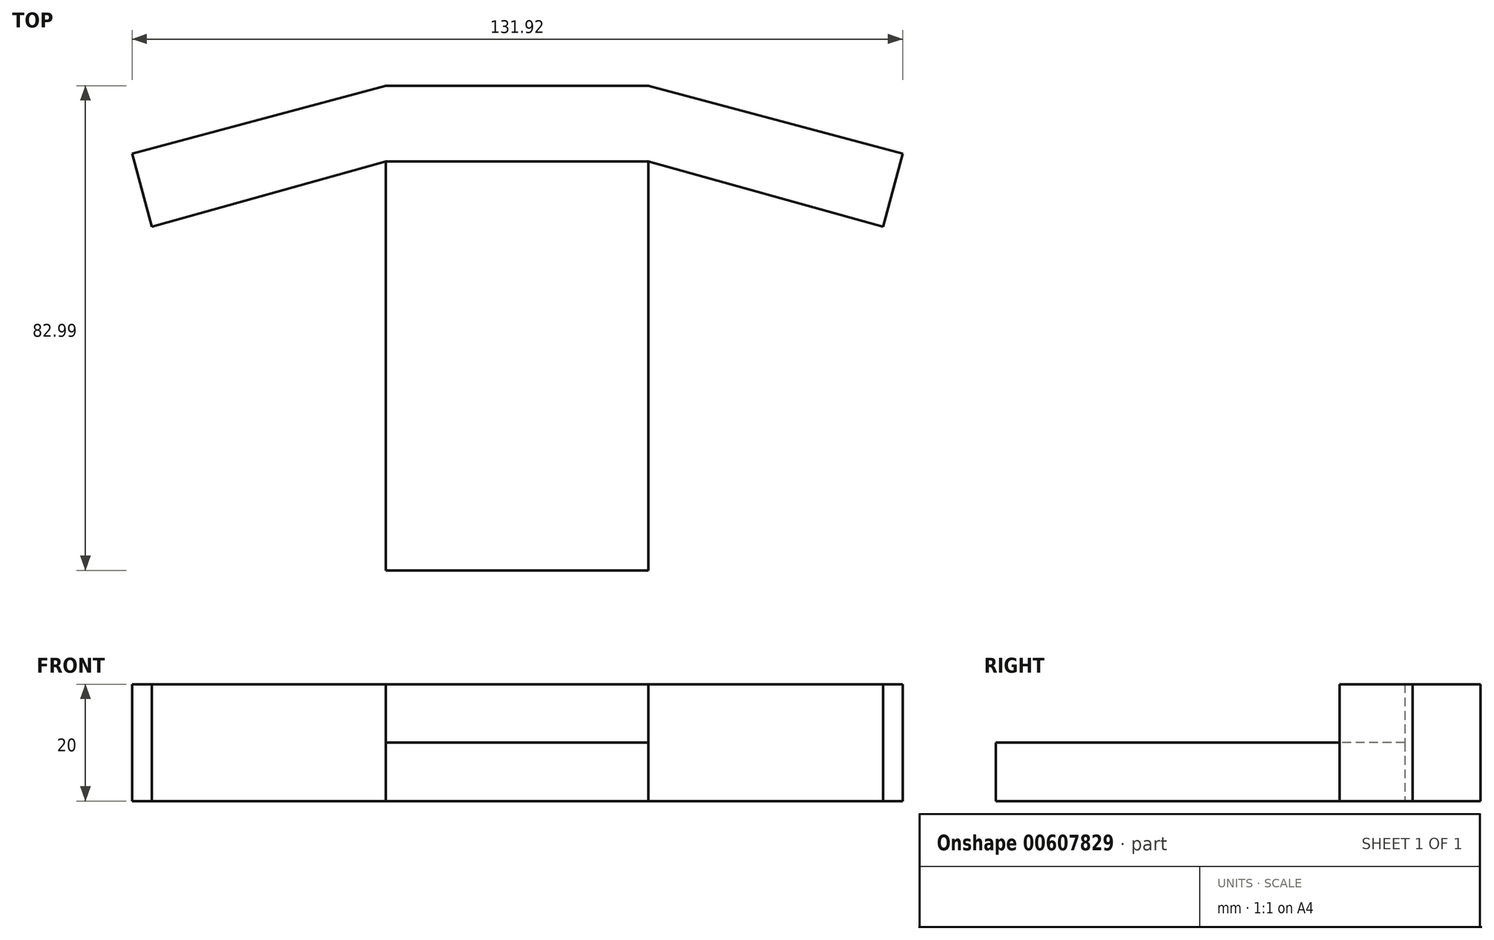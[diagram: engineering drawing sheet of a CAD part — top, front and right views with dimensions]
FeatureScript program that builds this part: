
annotation { "Feature Type Name" : "Feature", "Feature Type Description" : "" }
export const myFeature = defineFeature(function(context is Context, id is Id, definition is map)
    precondition{}
    {
        {
            var Q0;
            Q0=qCreatedBy(makeId("Top.planeOp"),FACE);
            var sketch = newSketch(context, id + "F0", { "sketchPlane" : qUnion([Q0])});
            skLineSegment(sketch, "E0", {"start": v(-65.94, 94.66) * mm, "end": v(-22.53, 106.3) * mm});
            skLineSegment(sketch, "E1", {"start": v(-22.53, 106.3) * mm, "end": v(22.47, 106.3) * mm});
            skLineSegment(sketch, "E2", {"start": v(22.47, 106.3) * mm, "end": v(65.98, 94.63) * mm});
            skLineSegment(sketch, "E3", {"start": v(-65.94, 94.66) * mm, "end": v(-62.58, 82.1) * mm});
            skLineSegment(sketch, "E4", {"start": v(-62.58, 82.1) * mm, "end": v(-22.53, 93.3) * mm});
            skLineSegment(sketch, "E5", {"start": v(65.98, 94.63) * mm, "end": v(62.62, 82.1) * mm});
            skLineSegment(sketch, "E6", {"start": v(22.47, 93.3) * mm, "end": v(62.62, 82.1) * mm});
            skLineSegment(sketch, "E7", {"start": v(-22.53, 93.3) * mm, "end": v(22.47, 93.3) * mm});
            skLineSegment(sketch, "E8", {"start": v(-22.53, 93.3) * mm, "end": v(-22.53, 23.3) * mm});
            skLineSegment(sketch, "E9", {"start": v(22.47, 93.3) * mm, "end": v(22.47, 23.3) * mm});
            skLineSegment(sketch, "E10", {"start": v(-22.53, 23.3) * mm, "end": v(22.47, 23.3) * mm});
            skSolve(sketch);
        }
        {
            var Q0;
            Q0=makeQuery(id+"F0.imprint","IMPRINT",FACE,{"disambiguationData":[TD([[makeQuery(id+"F0.imprint","IMPRINT",EDGE,{"derivedFrom":sQuery(id+"F0.wireOp",EDGE,"E7")}),-1.0]])]});
            var sketch = newSketch(context, id + "F1", { "sketchPlane" : qUnion([Q0])});
            skSolve(sketch);
        }
        {
            var Q0;
            Q0=makeQuery(id+"F0.imprint","IMPRINT",FACE,{"disambiguationData":[TD([[makeQuery(id+"F0.imprint","IMPRINT",EDGE,{"derivedFrom":sQuery(id+"F0.wireOp",EDGE,"E0")}),-1.0]])]});
            extrude(context, id + "F2", {"entities" : qUnion([Q0]), "depth" : 20 * mm, "offsetDistance" : 25 * mm});
        }
        {
            var Q0;
            Q0=makeQuery(id+"F1.imprint","IMPRINT",FACE,{"disambiguationData":[TD([[makeQuery(id+"F1.imprint","IMPRINT",EDGE,{"derivedFrom":makeQuery(id+"F0.imprint","IMPRINT",EDGE,{"derivedFrom":sQuery(id+"F0.wireOp",EDGE,"E7")})}),-1.0]])]});
            extrude(context, id + "F3", {"entities" : qUnion([Q0]), "operationType" : NewBodyOperationType.ADD, "depth" : 10 * mm, "offsetDistance" : 25 * mm});
        }
    });
